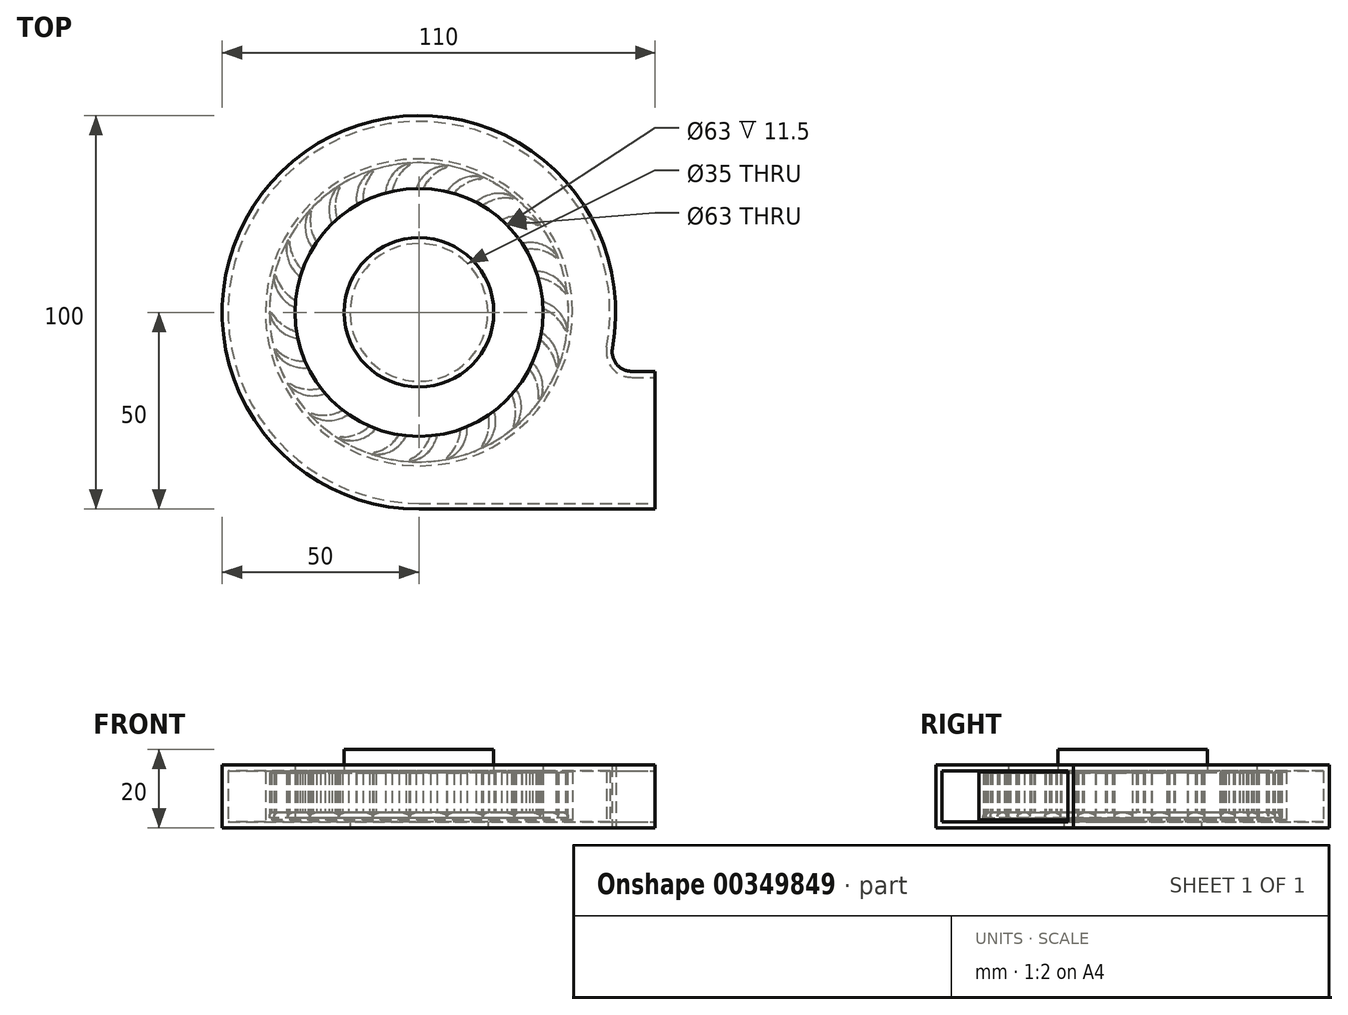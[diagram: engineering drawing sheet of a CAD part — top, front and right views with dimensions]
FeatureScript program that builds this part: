
annotation { "Feature Type Name" : "Feature", "Feature Type Description" : "" }
export const myFeature = defineFeature(function(context is Context, id is Id, definition is map)
    precondition{}
    {
        {
            var Q0;
            Q0=qCreatedBy(makeId("Top.planeOp"),FACE);
            var sketch = newSketch(context, id + "F0", { "sketchPlane" : qUnion([Q0])});
            skCircle(sketch, "E0", {"center": v(0, 0) * mm, "radius": 17.5 * mm});
            skCircle(sketch, "E1", {"center": v(0, 0) * mm, "radius": 38 * mm});
            skLineSegment(sketch, "E2.top", {"start": v(0, -50) * mm, "end": v(60, -50) * mm});
            skLineSegment(sketch, "E3.top", {"start": v(54.08, -15) * mm, "end": v(60, -15) * mm});
            skLineSegment(sketch, "E3.right", {"start": v(60, -50) * mm, "end": v(60, -15) * mm});
            skArc(sketch, "E4", {"start": v(49.17, -9.1) * mm, "mid": v(-31.98, 38.44) * mm, "end": v(0, -50) * mm});
            skCircle(sketch, "E5", {"center": v(0, 0) * mm, "radius": 31.5 * mm});
            skCircle(sketch, "E6", {"center": v(0, 0) * mm, "radius": 25 * mm, "construction": true});
            skPoint(sketch, "E7.visualSharp", {"position": v(47.7, -15) * mm});
            skArc(sketch, "E7.filletArc", {"start": v(49.17, -9.1) * mm, "mid": v(50.24, -13.2) * mm, "end": v(54.08, -15) * mm});
            skSolve(sketch);
        }
        {
            var Q0;
            Q0=qCreatedBy(makeId("Top.planeOp"),FACE);
            var sketch = newSketch(context, id + "F1", { "sketchPlane" : qUnion([Q0])});
            skArc(sketch, "E8", {"start": v(7, 37.1) * mm, "mid": v(1.04, 32.47) * mm, "end": v(0, 25) * mm, "construction": true});
            skArc(sketch, "E9", {"start": v(0.25, 25) * mm, "mid": v(0, 25) * mm, "end": v(-0.25, 25) * mm});
            skArc(sketch, "E10", {"start": v(7.05, 37.34) * mm, "mid": v(0.05, 33.15) * mm, "end": v(-0.25, 25) * mm});
            skArc(sketch, "E11", {"start": v(6.95, 36.85) * mm, "mid": v(1.42, 32.16) * mm, "end": v(0.25, 25) * mm});
            skLineSegment(sketch, "E12", {"start": v(7.05, 37.34) * mm, "end": v(6.95, 36.85) * mm});
            skLineSegment(sketch, "E13", {"start": v(0.05, 33.15) * mm, "end": v(1.42, 32.16) * mm, "construction": true});
            skPoint(sketch, "E14", {"position": v(1.78, 32.47) * mm});
            skPoint(sketch, "E14.positionSnap0", {"position": v(1.04, 32.47) * mm});
            skSolve(sketch);
        }
        {
            var Q0;
            Q0=qCreatedBy(makeId("Front.planeOp"),FACE);
            var sketch = newSketch(context, id + "F2", { "sketchPlane" : qUnion([Q0])});
            skLineSegment(sketch, "E15", {"start": v(0, 34.43) * mm, "end": v(0, -26.28) * mm});
            skSolve(sketch);
        }
        {
            var Q0;
            Q0=makeQuery(id+"F0.imprint","IMPRINT",FACE,{"disambiguationData":[TD([[makeQuery(id+"F0.imprint","IMPRINT",EDGE,{"derivedFrom":sQuery(id+"F0.wireOp",EDGE,"E1")}),1.0]])]});
            var Q1;
            Q1=makeQuery(id+"F0.imprint","IMPRINT",FACE,{"disambiguationData":[TD([[makeQuery(id+"F0.imprint","IMPRINT",EDGE,{"derivedFrom":sQuery(id+"F0.wireOp",EDGE,"E0")}),-1.0]])]});
            var Q2;
            Q2=makeQuery(id+"F0.imprint","IMPRINT",FACE,{"disambiguationData":[TD([[makeQuery(id+"F0.imprint","IMPRINT",EDGE,{"derivedFrom":sQuery(id+"F0.wireOp",EDGE,"E0")}),1.0]])]});
            extrude(context, id + "F3", {"entities" : qUnion([Q0, Q1, Q2]), "oppositeDirection" : true, "depth" : 1.5 * mm});
        }
        {
            var Q0;
            Q0=makeQuery(id+"F0.imprint","IMPRINT",FACE,{"disambiguationData":[TD([[makeQuery(id+"F0.imprint","IMPRINT",EDGE,{"derivedFrom":sQuery(id+"F0.wireOp",EDGE,"E0")}),1.0]])]});
            extrude(context, id + "F4", {"entities" : qUnion([Q0]), "operationType" : NewBodyOperationType.ADD, "depth" : 15 * mm});
        }
        {
            var Q0;
            Q0=makeQuery(id+"F3.opExtrude","CAP_FACE",FACE,{"disambiguationData":[OSD([sQuery(id+"F0.wireOp",EDGE,"E1")])],"isStart":false});
            shell(context, id + "F5", {"entities" : qUnion([Q0]), "thickness" : 1.5 * mm});
        }
        {
            var Q0;
            Q0=makeQuery(id+"F4.opExtrude","CAP_EDGE",EDGE,{"disambiguationData":[OSD([sQuery(id+"F0.wireOp",EDGE,"E0")])],"isStart":false});
            var Q1;
            Q1=makeQuery(id+"F3.opExtrude","CAP_EDGE",EDGE,{"disambiguationData":[OSD([sQuery(id+"F0.wireOp",EDGE,"E1")])],"isStart":true});
            var Q2;
            Q2=makeQuery(id+"F4.opExtrude","CAP_EDGE",EDGE,{"disambiguationData":[OSD([sQuery(id+"F0.wireOp",EDGE,"E0")])],"isStart":true});
            fillet(context, id + "F6", {"entities" : qUnion([Q0, Q1, Q2]), "radius" : 1 * mm, "tangentPropagation" : true, "allowEdgeOverflow" : false});
        }
        {
            var Q0;
            {var subQ0=sQuery(id+"F0.wireOp",EDGE,"E0");Q0=makeQuery(id+"F5.opShell","OFFSET_EDGE",EDGE,{"disambiguationData":[OSD([subQ0]),TDD([makeQuery(id+"F4.opExtrude","CAP_EDGE",EDGE,{"disambiguationData":[OSD([subQ0])],"isStart":true})])]});}
            fillet(context, id + "F7", {"entities" : qUnion([Q0]), "radius" : 2.5 * mm, "tangentPropagation" : true, "allowEdgeOverflow" : false});
        }
        {
            var Q0;
            Q0 = qSketchRegion(id + "F1", true);
            extrude(context, id + "F8", {"entities" : qUnion([Q0]), "depth" : 10 * mm, "hasSecondDirection" : true, "secondDirectionOppositeDirection" : true, "secondDirectionDepth" : 1 * mm});
        }
        {
            var Q0;
            Q0=makeQuery(id+"F8.opExtrude","SWEPT_BODY",BODY,{"disambiguationData":[OSD([sQuery(id+"F1.wireOp",EDGE,"E9"),sQuery(id+"F1.wireOp",EDGE,"E10"),sQuery(id+"F1.wireOp",EDGE,"E11"),sQuery(id+"F1.wireOp",EDGE,"E12")])]});
            var Q1;
            Q1=sQuery(id+"F2.wireOp",EDGE,"E15");
            circularPattern(context, id + "F9", {"operationType" : NewBodyOperationType.ADD, "entities" : qUnion([Q0]), "axis" : qUnion([Q1]), "angle" : 360 * degree, "instanceCount" : 25, "equalSpace" : true});
        }
        {
            var Q0;
            Q0=makeQuery(id+"F0.imprint","IMPRINT",FACE,{"disambiguationData":[TD([[makeQuery(id+"F0.imprint","IMPRINT",EDGE,{"derivedFrom":sQuery(id+"F0.wireOp",EDGE,"E1")}),-1.0]])]});
            var Q1;
            Q1=makeQuery(id+"F0.imprint","IMPRINT",FACE,{"disambiguationData":[TD([[makeQuery(id+"F0.imprint","IMPRINT",EDGE,{"derivedFrom":sQuery(id+"F0.wireOp",EDGE,"E0")}),-1.0]])]});
            var Q2;
            Q2=makeQuery(id+"F0.imprint","IMPRINT",FACE,{"disambiguationData":[TD([[makeQuery(id+"F0.imprint","IMPRINT",EDGE,{"derivedFrom":sQuery(id+"F0.wireOp",EDGE,"E1")}),1.0]])]});
            extrude(context, id + "F10", {"entities" : qUnion([Q0, Q1, Q2]), "depth" : 12 * mm, "hasSecondDirection" : true, "secondDirectionOppositeDirection" : true, "secondDirectionDepth" : 4 * mm});
        }
        {
            var Q0;
            Q0=makeQuery(id+"F10.opExtrude","SWEPT_FACE",FACE,{"disambiguationData":[OSD([sQuery(id+"F0.wireOp",EDGE,"E3.right")])]});
            shell(context, id + "F11", {"entities" : qUnion([Q0]), "thickness" : 1.5 * mm});
        }
        {
            var Q0;
            Q0=makeQuery(id+"F0.imprint","IMPRINT",FACE,{"disambiguationData":[TD([[makeQuery(id+"F0.imprint","IMPRINT",EDGE,{"derivedFrom":sQuery(id+"F0.wireOp",EDGE,"E0")}),-1.0]])]});
            var Q1;
            Q1=makeQuery(id+"F0.imprint","IMPRINT",FACE,{"disambiguationData":[TD([[makeQuery(id+"F0.imprint","IMPRINT",EDGE,{"derivedFrom":sQuery(id+"F0.wireOp",EDGE,"E0")}),1.0]])]});
            extrude(context, id + "F12", {"entities" : qUnion([Q0, Q1]), "operationType" : NewBodyOperationType.REMOVE, "depth" : 25 * mm, "hasSecondDirection" : true, "secondDirectionOppositeDirection" : true, "secondDirectionDepth" : 2.5 * mm});
        }
        {
            var Q0;
            Q0=qCreatedBy(makeId("Top.planeOp"),FACE);
            var sketch = newSketch(context, id + "F13", { "sketchPlane" : qUnion([Q0])});
            skCircle(sketch, "E16", {"center": v(0, 0) * mm, "radius": 39 * mm});
            skCircle(sketch, "E17", {"center": v(0, 0) * mm, "radius": 19 * mm});
            skSolve(sketch);
        }
        {
            var Q0;
            Q0 = qSketchRegion(id + "F13", true);
            var Q1;
            Q1=makeQuery(id+"F13.imprint","IMPRINT",FACE,{"disambiguationData":[TD([[makeQuery(id+"F13.imprint","IMPRINT",EDGE,{"derivedFrom":sQuery(id+"F13.wireOp",EDGE,"E17")}),1.0]])]});
            extrude(context, id + "F14", {"entities" : qUnion([Q0, Q1]), "depth" : 10.2 * mm, "hasSecondDirection" : true, "secondDirectionOppositeDirection" : true, "secondDirectionDepth" : 2 * mm});
        }
        {
            var Q0;
            Q0=makeQuery(id+"F13.imprint","IMPRINT",FACE,{"disambiguationData":[TD([[makeQuery(id+"F13.imprint","IMPRINT",EDGE,{"derivedFrom":sQuery(id+"F13.wireOp",EDGE,"E17")}),1.0]])]});
            var Q1;
            Q1=sQuery(id+"F13.wireOp",EDGE,"E17");
            extrude(context, id + "F15", {"entities" : qUnion([Q0]), "operationType" : NewBodyOperationType.ADD, "surfaceEntities" : qUnion([Q1]), "depth" : 16 * mm});
        }
    });
